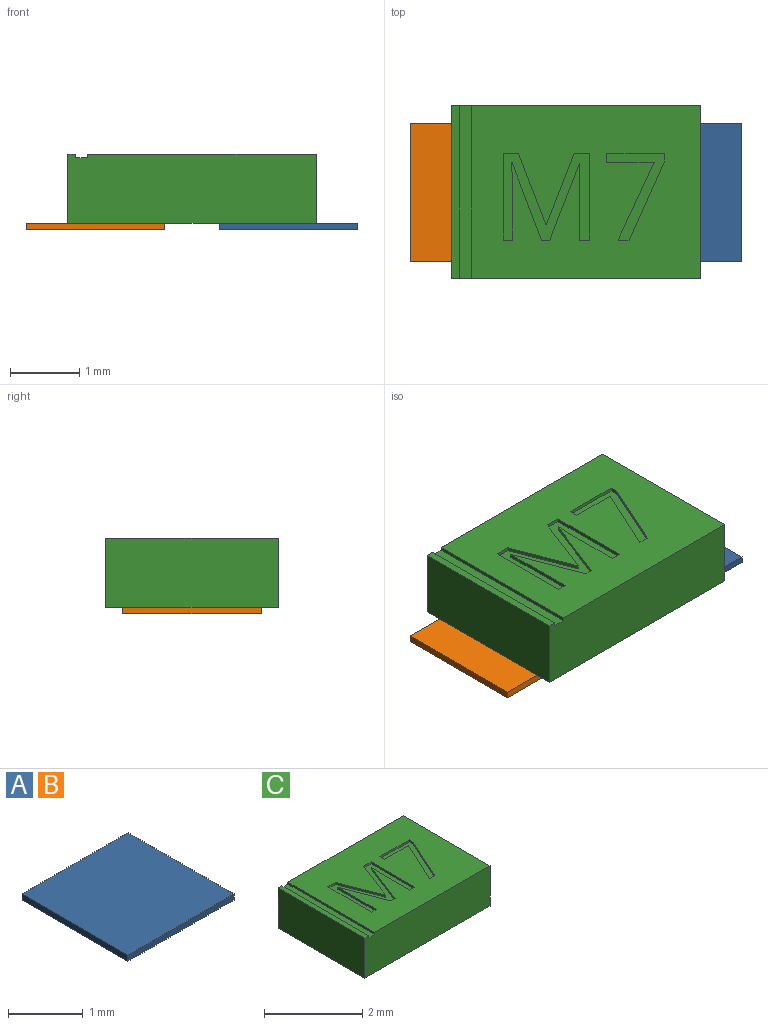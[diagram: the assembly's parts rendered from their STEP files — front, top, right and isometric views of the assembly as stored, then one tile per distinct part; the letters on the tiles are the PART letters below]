
ASSEMBLY  parts=3 mates=2
PART A: 6 faces, bbox 2x2x0.1 mm
  f0: plane 2x0.1mm, normal (0,1,0), area 0.2mm2, adj f1,f3,f4,f5
  f1: plane 2x0.1mm, normal (-1,0,0), area 0.2mm2, adj f0,f2,f4,f5
  f2: plane 2x0.1mm, normal (0,-1,0), area 0.2mm2, adj f1,f3,f4,f5
  f3: plane 2x0.1mm, normal (1,0,0), area 0.2mm2, adj f0,f2,f4,f5
  f4: plane 2x2mm, normal (0,0,1), area 4mm2, adj f0,f1,f2,f3
  f5: plane 2x2mm, normal (0,0,-1), area 4mm2, adj f0,f1,f2,f3
PART B: same geometry as A
PART C: 37 faces, bbox 3.6x2.5x1 mm
  f0: plane 3.6x1mm, normal (0,1,0), area 3.6mm2, adj f1,f2,f3,f5,f6,f34,f35,f36
  f1: plane 3.31x2.5mm, normal (0,0,1), area 7.3mm2, adj f0,f4,f5,f7,f8,f9,f10,f11
  f2: plane 2.5x0.11mm, normal (0,0,1), area 0.3mm2, adj f0,f3,f4,f34
  f3: plane 2.5x1mm, normal (-1,0,0), area 2.5mm2, adj f0,f2,f4,f6
  f4: plane 3.6x1mm, normal (0,-1,0), area 3.6mm2, adj f1,f2,f3,f5,f6,f34,f35,f36
  f5: plane 2.5x1mm, normal (1,0,0), area 2.5mm2, adj f0,f1,f4,f6
  f6: plane 3.6x2.5mm, normal (0,0,-1), area 9mm2, adj f0,f3,f4,f5
  f7: plane 1.12x0.43mm, normal (0.93,0.36,0), area 0.1mm2, adj f1,f8,f24,f25
  f8: plane 0.12x0.05mm, normal (0,1,0), area 0mm2, adj f1,f7,f9,f25
  f9: plane 1.11x0.43mm, normal (-0.93,0.36,0), area 0.1mm2, adj f1,f8,f10,f25
  f10: plane 0.05x0.01mm, normal (0,1,0), area 0mm2, adj f1,f9,f11,f25
  f11: extruded ~0.3x0.05mm, area 0mm2, adj f1,f10,f12,f25
  f12: plane 0.81x0.05mm, normal (1,0,0), area 0mm2, adj f1,f11,f13,f25
  f13: plane 0.15x0.05mm, normal (0,1,0), area 0mm2, adj f1,f12,f14,f25
  f14: plane 1.26x0.05mm, normal (-1,0,0), area 0.1mm2, adj f1,f13,f15,f25
  f15: plane 0.22x0.05mm, normal (0,-1,0), area 0mm2, adj f1,f14,f16,f25
  f16: plane 1.04x0.4mm, normal (0.93,-0.36,0), area 0.1mm2, adj f1,f15,f17,f25
  f17: plane 0.05x0.01mm, normal (0,-1,0), area 0mm2, adj f1,f16,f18,f25
  f18: plane 1.04x0.4mm, normal (-0.93,-0.36,0), area 0.1mm2, adj f1,f17,f19,f25
  f19: plane 0.22x0.05mm, normal (0,-1,0), area 0mm2, adj f1,f18,f20,f25
  f20: plane 1.26x0.05mm, normal (1,0,0), area 0.1mm2, adj f1,f19,f21,f25
  f21: plane 0.14x0.05mm, normal (0,1,0), area 0mm2, adj f1,f20,f22,f25
  f22: plane 0.8x0.05mm, normal (-1,0,0), area 0mm2, adj f1,f21,f23,f25
  f23: extruded ~0.32x0.05mm, area 0mm2, adj f1,f22,f24,f25
  f24: plane 0.05x0.01mm, normal (0,1,0), area 0mm2, adj f1,f7,f23,f25
  f25: plane 1.26x1.25mm, normal (0,0,1), area 0.7mm2, adj f7,f8,f9,f10,f11,f12,f13,f14
  f26: plane 1.13x0.52mm, normal (0.91,-0.42,0), area 0.1mm2, adj f1,f27,f32,f33
  f27: plane 0.16x0.05mm, normal (0,1,0), area 0mm2, adj f1,f26,f28,f33
  f28: plane 1.14x0.52mm, normal (-0.91,0.41,0), area 0.1mm2, adj f1,f27,f29,f33
  f29: plane 0.11x0.05mm, normal (-1,0,0), area 0mm2, adj f1,f28,f30,f33
  f30: plane 0.84x0.05mm, normal (0,-1,0), area 0mm2, adj f1,f29,f31,f33
  f31: plane 0.13x0.05mm, normal (1,0,0), area 0mm2, adj f1,f30,f32,f33
  f32: plane 0.69x0.05mm, normal (0,1,0), area 0mm2, adj f1,f26,f31,f33
  f33: plane 1.26x0.84mm, normal (0,0,1), area 0.3mm2, adj f26,f27,f28,f29,f30,f31,f32
  f34: plane 2.5x0.05mm, normal (1,0,0), area 0.1mm2, adj f0,f2,f4,f36
  f35: plane 2.5x0.05mm, normal (-1,0,0), area 0.1mm2, adj f0,f1,f4,f36
  f36: plane 2.5x0.17mm, normal (0,0,1), area 0.4mm2, adj f0,f4,f34,f35
PLACE A at identity
PLACE B t=(-2.8,0,0)mm
PLACE C t=(20.73,-1.93,0.1)mm
MATE fastened B.f4 <-> C.f6  axis (0,0,1) through (-27.68,2.1,0.1)mm
MATE fastened C.f6 <-> A.f4  axis (0,0,-1) through (-23.48,2.1,0.1)mm
